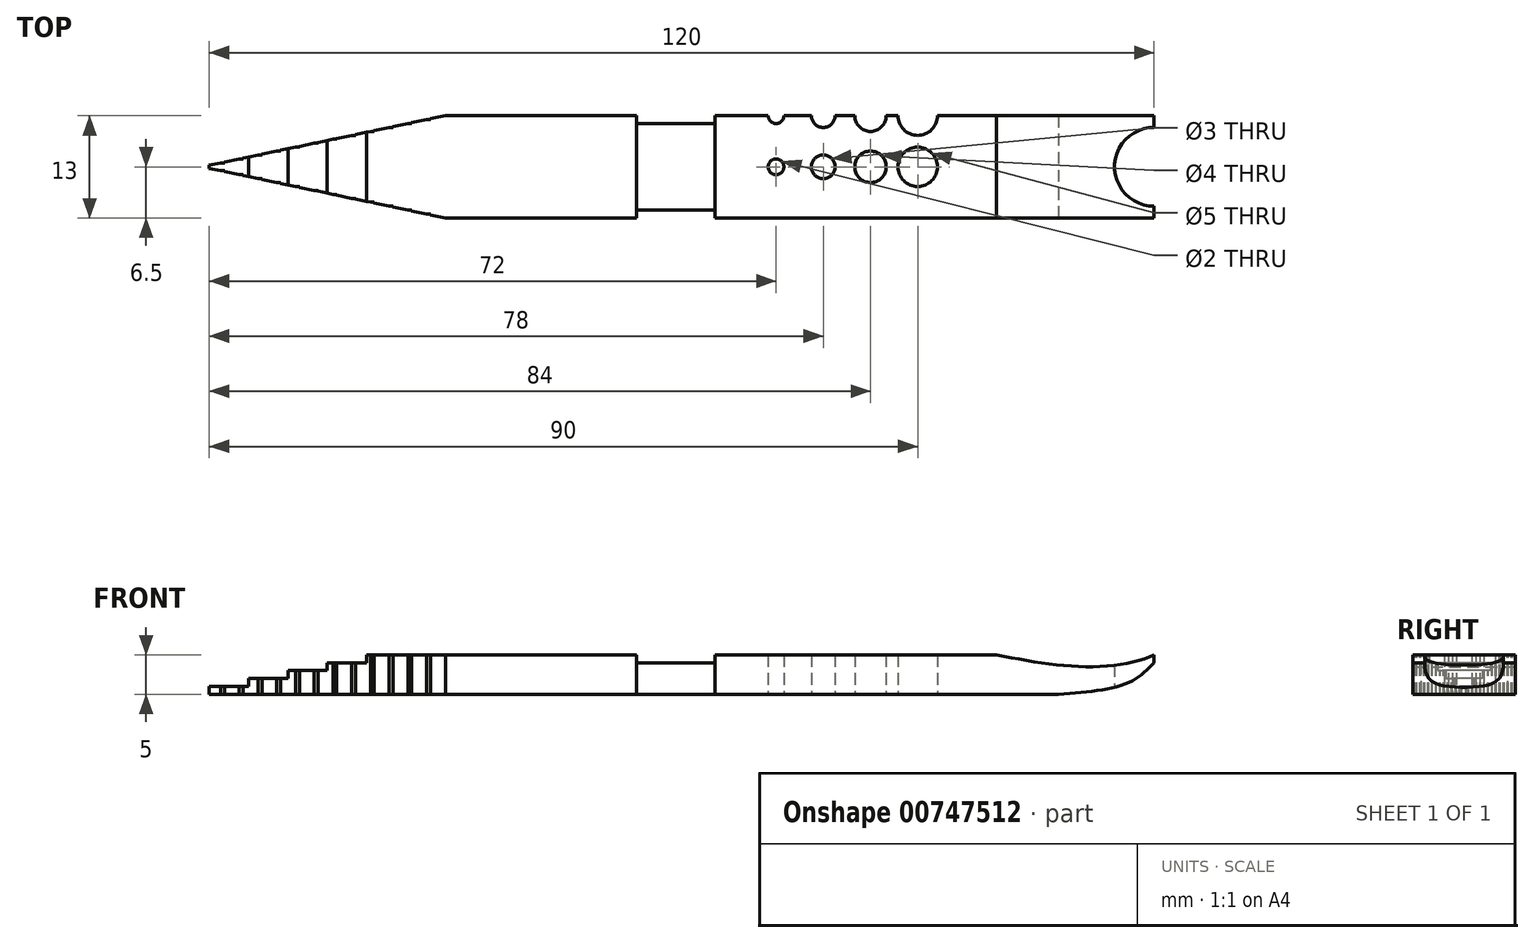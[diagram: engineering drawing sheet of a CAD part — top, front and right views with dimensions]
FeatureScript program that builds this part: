
annotation { "Feature Type Name" : "Feature", "Feature Type Description" : "" }
export const myFeature = defineFeature(function(context is Context, id is Id, definition is map)
    precondition{}
    {
        {
            var Q0;
            Q0=qCreatedBy(makeId("Top.planeOp"),FACE);
            var sketch = newSketch(context, id + "F0", { "sketchPlane" : qUnion([Q0])});
            skLineSegment(sketch, "E0.bottom", {"start": v(0, 0) * mm, "end": v(-20, 0) * mm});
            skLineSegment(sketch, "E0.top", {"start": v(0, -13) * mm, "end": v(-20, -13) * mm});
            skLineSegment(sketch, "E0.left", {"start": v(0, 0) * mm, "end": v(0, -13) * mm});
            skLineSegment(sketch, "E0.right", {"start": v(-20, 0) * mm, "end": v(-20, -13) * mm});
            skLineSegment(sketch, "E1.bottom", {"start": v(0, 0) * mm, "end": v(51, 0) * mm});
            skLineSegment(sketch, "E1.top", {"start": v(0, -13) * mm, "end": v(80, -13) * mm});
            skLineSegment(sketch, "E1.right", {"start": v(80, 0) * mm, "end": v(80, -13) * mm});
            skLineSegment(sketch, "E2.bottom", {"start": v(80, 0) * mm, "end": v(100, 0) * mm});
            skLineSegment(sketch, "E2.top", {"start": v(80, -13) * mm, "end": v(100, -13) * mm});
            skLineSegment(sketch, "E2.right", {"start": v(100, 0) * mm, "end": v(100, -1.5) * mm});
            skLineSegment(sketch, "E3", {"start": v(0, -6.5) * mm, "end": v(80, -6.5) * mm, "construction": true});
            skLineSegment(sketch, "E4.0", {"start": v(70, 0) * mm, "end": v(70, -13) * mm, "construction": true});
            skLineSegment(sketch, "E5.0", {"start": v(64, 0) * mm, "end": v(64, -13) * mm, "construction": true});
            skLineSegment(sketch, "E6.0", {"start": v(58, 0) * mm, "end": v(58, -13) * mm, "construction": true});
            skLineSegment(sketch, "E7.0", {"start": v(52, 0) * mm, "end": v(52, -13) * mm, "construction": true});
            skCircle(sketch, "E8", {"center": v(70, -6.5) * mm, "radius": 2.5 * mm});
            skCircle(sketch, "E9", {"center": v(64, -6.5) * mm, "radius": 2 * mm});
            skCircle(sketch, "E10", {"center": v(58, -6.5) * mm, "radius": 1.5 * mm});
            skCircle(sketch, "E11", {"center": v(52, -6.5) * mm, "radius": 1 * mm});
            skArc(sketch, "E12", {"start": v(67.5, 0) * mm, "mid": v(70, -2.5) * mm, "end": v(72.5, 0) * mm});
            skArc(sketch, "E13", {"start": v(62, 0) * mm, "mid": v(64, -2) * mm, "end": v(66, 0) * mm});
            skArc(sketch, "E14", {"start": v(56.5, 0) * mm, "mid": v(58, -1.5) * mm, "end": v(59.5, 0) * mm});
            skArc(sketch, "E15", {"start": v(51, 0) * mm, "mid": v(52, -1) * mm, "end": v(53, 0) * mm});
            skLineSegment(sketch, "E16.trimOffspring", {"start": v(72.5, 0) * mm, "end": v(80, 0) * mm});
            skLineSegment(sketch, "E17.trimOffspring", {"start": v(66, 0) * mm, "end": v(67.5, 0) * mm});
            skLineSegment(sketch, "E18.trimOffspring", {"start": v(59.5, 0) * mm, "end": v(62, 0) * mm});
            skLineSegment(sketch, "E19.trimOffspring", {"start": v(53, 0) * mm, "end": v(56.5, 0) * mm});
            skArc(sketch, "E20", {"start": v(100, -1.5) * mm, "mid": v(95, -6.5) * mm, "end": v(100, -11.5) * mm});
            skLineSegment(sketch, "E21.trimOffspring", {"start": v(100, -11.5) * mm, "end": v(100, -13) * mm});
            skSolve(sketch);
        }
        {
            var Q0;
            Q0=makeQuery(id+"F0.imprint","IMPRINT",FACE,{"disambiguationData":[TD([[makeQuery(id+"F0.imprint","IMPRINT",EDGE,{"derivedFrom":sQuery(id+"F0.wireOp",EDGE,"E1.bottom")}),-1.0]])]});
            var Q1;
            Q1=makeQuery(id+"F0.imprint","IMPRINT",FACE,{"disambiguationData":[TD([[makeQuery(id+"F0.imprint","IMPRINT",EDGE,{"derivedFrom":sQuery(id+"F0.wireOp",EDGE,"E0.bottom")}),1.0]])]});
            extrude(context, id + "F1", {"entities" : qUnion([Q0, Q1]), "depth" : 5 * mm, "offsetDistance" : 25 * mm});
        }
        {
            var Q0;
            Q0=makeQuery(id+"F0.imprint","IMPRINT",FACE,{"disambiguationData":[TD([[makeQuery(id+"F0.imprint","IMPRINT",EDGE,{"derivedFrom":sQuery(id+"F0.wireOp",EDGE,"E2.bottom")}),-1.0]])]});
            extrude(context, id + "F2", {"entities" : qUnion([Q0]), "operationType" : NewBodyOperationType.ADD, "depth" : 5 * mm, "offsetDistance" : 25 * mm});
        }
        {
            var Q0;
            Q0=makeQuery(id+"F2.boolean.opBoolean","MERGE",FACE,{"derivedFrom":[makeQuery(id+"F1.opExtrude","SWEPT_FACE",FACE,{"disambiguationData":[OSD([sQuery(id+"F0.wireOp",EDGE,"E0.top"),sQuery(id+"F0.wireOp",EDGE,"E1.top")])]}),makeQuery(id+"F2.opExtrude","SWEPT_FACE",FACE,{"disambiguationData":[OSD([sQuery(id+"F0.wireOp",EDGE,"E2.top")])]})]});
            var sketch = newSketch(context, id + "F3", { "sketchPlane" : qUnion([Q0])});
            skLineSegment(sketch, "E22", {"start": v(5, 5) * mm, "end": v(0, 5) * mm});
            skLineSegment(sketch, "E23", {"start": v(0, 5) * mm, "end": v(0, 4) * mm});
            skLineSegment(sketch, "E24", {"start": v(0, 4) * mm, "end": v(-5, 4) * mm});
            skLineSegment(sketch, "E25", {"start": v(-5, 4) * mm, "end": v(-5, 3) * mm});
            skLineSegment(sketch, "E26", {"start": v(-5, 3) * mm, "end": v(-10, 3) * mm});
            skLineSegment(sketch, "E27", {"start": v(-10, 3) * mm, "end": v(-10, 2) * mm});
            skLineSegment(sketch, "E28", {"start": v(-10, 2) * mm, "end": v(-15, 2) * mm});
            skLineSegment(sketch, "E29", {"start": v(-15, 2) * mm, "end": v(-15, 1) * mm});
            skLineSegment(sketch, "E30", {"start": v(-15, 1) * mm, "end": v(-20, 1) * mm});
            skLineSegment(sketch, "E31", {"start": v(-20, 1) * mm, "end": v(-20, 0) * mm});
            skLineSegment(sketch, "E32", {"start": v(-20, 0) * mm, "end": v(0, 0) * mm});
            skLineSegment(sketch, "E33", {"start": v(0, 0) * mm, "end": v(0, -1.18) * mm});
            skLineSegment(sketch, "E34", {"start": v(0, -1.18) * mm, "end": v(-22.5, -1.18) * mm});
            skLineSegment(sketch, "E35", {"start": v(-22.5, -1.18) * mm, "end": v(-22.5, 6.94) * mm});
            skLineSegment(sketch, "E36", {"start": v(-22.5, 6.94) * mm, "end": v(5, 6.94) * mm});
            skLineSegment(sketch, "E37", {"start": v(5, 6.94) * mm, "end": v(5, 5) * mm});
            skLineSegment(sketch, "E38", {"start": v(0, 0) * mm, "end": v(80, 0) * mm, "construction": true});
            skLineSegment(sketch, "E39", {"start": v(80, 0) * mm, "end": v(80, 5) * mm, "construction": true});
            skFitSpline(sketch, "E40", {"points": [v(80, 5) * mm, v(91.86, 3.5) * mm, v(100, 5) * mm, v(102.7, 7.03) * mm], "startDerivative": vector(28.47, -5.44) * mm, "endDerivative": vector(9.91, 9.63) * mm});
            skLineSegment(sketch, "E41", {"start": v(100, 5) * mm, "end": v(100, 4) * mm});
            skLineSegment(sketch, "E42", {"start": v(80, 0) * mm, "end": v(87.86, 0) * mm});
            skFitSpline(sketch, "E43", {"points": [v(87.86, 0) * mm, v(96.6, 1.4) * mm, v(100, 4) * mm, v(102.7, 7.03) * mm], "startDerivative": vector(23.43, 1.75) * mm, "endDerivative": vector(9.4, 10.76) * mm});
            skLineSegment(sketch, "E44", {"start": v(80, 5) * mm, "end": v(80, 7.9) * mm});
            skLineSegment(sketch, "E45", {"start": v(80, 7.9) * mm, "end": v(104.35, 7.9) * mm});
            skLineSegment(sketch, "E46", {"start": v(104.35, 7.9) * mm, "end": v(104.35, -1.83) * mm});
            skLineSegment(sketch, "E47", {"start": v(104.35, -1.83) * mm, "end": v(80, -1.83) * mm});
            skLineSegment(sketch, "E48", {"start": v(80, 0) * mm, "end": v(80, -1.83) * mm});
            skSolve(sketch);
        }
        {
            var Q0;
            {var subQ0=sQuery(id+"F3.wireOp",EDGE,"E41");Q0=makeQuery(id+"F3.imprint","IMPRINT",FACE,{"disambiguationData":[TD([[makeQuery(id+"F3.imprint","IMPRINT",EDGE,{"derivedFrom":subQ0}),1.0]])]});}
            var Q1;
            {var subQ0=sQuery(id+"F3.wireOp",EDGE,"E23");Q1=makeQuery(id+"F3.imprint","IMPRINT",FACE,{"disambiguationData":[TD([[makeQuery(id+"F3.imprint","IMPRINT",EDGE,{"derivedFrom":subQ0}),-1.0]])]});}
            var Q2;
            {var subQ0=sQuery(id+"F3.wireOp",EDGE,"E40");var subQ1=makeQuery(id+"F2.boolean.opBoolean","MERGE",EDGE,{"derivedFrom":[makeQuery(id+"F1.opExtrude","CAP_EDGE",EDGE,{"disambiguationData":[OSD([sQuery(id+"F0.wireOp",EDGE,"E0.top"),sQuery(id+"F0.wireOp",EDGE,"E1.top")])],"isStart":false}),makeQuery(id+"F2.opExtrude","CAP_EDGE",EDGE,{"disambiguationData":[OSD([sQuery(id+"F0.wireOp",EDGE,"E2.top")])],"isStart":false})]});var subQ2=makeQuery(id+"F3.imprint","INTERSECT",VERTEX,{"derivedFrom":[subQ1,subQ0,sQuery(id+"F3.wireOp",EDGE,"E41")]});Q2=makeQuery(id+"F3.imprint","IMPRINT",FACE,{"disambiguationData":[TD([[makeQuery(id+"F3.imprint","IMPRINT",EDGE,{"disambiguationData":[TD([[subQ2,1.0]])],"derivedFrom":subQ0}),1.0]])]});}
            var Q3;
            {var subQ0=sQuery(id+"F3.wireOp",EDGE,"E43");var subQ1=sQuery(id+"F0.wireOp",EDGE,"E2.top");var subQ2=makeQuery(id+"F2.opExtrude","SWEPT_EDGE",EDGE,{"disambiguationData":[OSD([subQ1,sQuery(id+"F0.wireOp",EDGE,"E21.trimOffspring")])]});var subQ3=makeQuery(id+"F3.imprint","INTERSECT",VERTEX,{"derivedFrom":[subQ2,sQuery(id+"F3.wireOp",EDGE,"E41"),subQ0]});Q3=makeQuery(id+"F3.imprint","IMPRINT",FACE,{"disambiguationData":[TD([[makeQuery(id+"F3.imprint","IMPRINT",EDGE,{"disambiguationData":[TD([[subQ3,1.0]])],"derivedFrom":subQ0}),-1.0]])]});}
            extrude(context, id + "F4", {"entities" : qUnion([Q0, Q1, Q2, Q3]), "operationType" : NewBodyOperationType.REMOVE, "oppositeDirection" : true, "depth" : 25 * mm, "offsetDistance" : 25 * mm});
        }
        {
            var Q0;
            Q0=makeQuery(id+"F4.boolean.opBoolean","COPY",FACE,{"derivedFrom":makeQuery(id+"F4.opExtrude","SWEPT_FACE",FACE,{"disambiguationData":[OSD([sQuery(id+"F3.wireOp",EDGE,"E30")])]})});
            var sketch = newSketch(context, id + "F5", { "sketchPlane" : qUnion([Q0])});
            skLineSegment(sketch, "E49", {"start": v(10, -6.5) * mm, "end": v(10, 0) * mm, "construction": true});
            skLineSegment(sketch, "E50", {"start": v(10, -6.5) * mm, "end": v(10, -13) * mm, "construction": true});
            skLineSegment(sketch, "E51", {"start": v(10, 0) * mm, "end": v(8.12, -0.4) * mm});
            skLineSegment(sketch, "E52", {"start": v(10, 0) * mm, "end": v(10, 3.1) * mm});
            skLineSegment(sketch, "E53", {"start": v(10, 3.1) * mm, "end": v(-21.73, 3.1) * mm});
            skLineSegment(sketch, "E54", {"start": v(-21.73, 3.1) * mm, "end": v(-21.73, -15.95) * mm});
            skLineSegment(sketch, "E55", {"start": v(-21.73, -15.95) * mm, "end": v(10, -15.95) * mm});
            skLineSegment(sketch, "E56", {"start": v(10, -15.95) * mm, "end": v(10, -13) * mm});
            skLineSegment(sketch, "E57", {"start": v(-18.57, -6) * mm, "end": v(-18.07, -6) * mm});
            skLineSegment(sketch, "E58", {"start": v(-18.07, -6) * mm, "end": v(-18.07, -5.9) * mm});
            skLineSegment(sketch, "E59", {"start": v(-16.2, -5.5) * mm, "end": v(-15.7, -5.5) * mm});
            skLineSegment(sketch, "E60", {"start": v(-15.7, -5.5) * mm, "end": v(-15.7, -5.4) * mm});
            skLineSegment(sketch, "E61", {"start": v(-13.8, -5) * mm, "end": v(-13.3, -5) * mm});
            skLineSegment(sketch, "E62", {"start": v(-13.3, -5) * mm, "end": v(-13.3, -4.9) * mm});
            skLineSegment(sketch, "E63", {"start": v(-11.43, -4.5) * mm, "end": v(-10.93, -4.5) * mm});
            skLineSegment(sketch, "E64", {"start": v(-10.93, -4.5) * mm, "end": v(-10.93, -4.4) * mm});
            skLineSegment(sketch, "E65", {"start": v(-9.05, -4) * mm, "end": v(-8.55, -4) * mm});
            skLineSegment(sketch, "E66", {"start": v(-8.55, -4) * mm, "end": v(-8.55, -3.9) * mm});
            skLineSegment(sketch, "E67", {"start": v(-6.67, -3.5) * mm, "end": v(-6.17, -3.5) * mm});
            skLineSegment(sketch, "E68", {"start": v(-6.17, -3.5) * mm, "end": v(-6.17, -3.4) * mm});
            skLineSegment(sketch, "E69", {"start": v(-4.29, -3) * mm, "end": v(-3.79, -3) * mm});
            skLineSegment(sketch, "E70", {"start": v(-3.79, -3) * mm, "end": v(-3.79, -2.9) * mm});
            skLineSegment(sketch, "E71", {"start": v(-1.9, -2.5) * mm, "end": v(-1.4, -2.5) * mm});
            skLineSegment(sketch, "E72", {"start": v(-1.4, -2.5) * mm, "end": v(-1.4, -2.4) * mm});
            skLineSegment(sketch, "E73", {"start": v(0.48, -2) * mm, "end": v(0.98, -2) * mm});
            skLineSegment(sketch, "E74", {"start": v(0.98, -2) * mm, "end": v(0.98, -1.9) * mm});
            skLineSegment(sketch, "E75", {"start": v(2.86, -1.5) * mm, "end": v(3.36, -1.5) * mm});
            skLineSegment(sketch, "E76", {"start": v(3.36, -1.5) * mm, "end": v(3.36, -1.4) * mm});
            skLineSegment(sketch, "E77", {"start": v(5.24, -1) * mm, "end": v(5.74, -1) * mm});
            skLineSegment(sketch, "E78", {"start": v(5.74, -1) * mm, "end": v(5.74, -0.9) * mm});
            skLineSegment(sketch, "E79", {"start": v(7.62, -0.5) * mm, "end": v(8.12, -0.5) * mm});
            skLineSegment(sketch, "E80", {"start": v(8.12, -0.5) * mm, "end": v(8.12, -0.4) * mm});
            skLineSegment(sketch, "E81.trimOffspring", {"start": v(7.62, -0.5) * mm, "end": v(5.74, -0.9) * mm});
            skLineSegment(sketch, "E82.trimOffspring", {"start": v(5.24, -1) * mm, "end": v(3.36, -1.4) * mm});
            skLineSegment(sketch, "E83.trimOffspring", {"start": v(2.86, -1.5) * mm, "end": v(0.98, -1.9) * mm});
            skLineSegment(sketch, "E84.trimOffspring", {"start": v(0.48, -2) * mm, "end": v(-1.4, -2.4) * mm});
            skLineSegment(sketch, "E85.trimOffspring", {"start": v(-1.9, -2.5) * mm, "end": v(-3.79, -2.9) * mm});
            skLineSegment(sketch, "E86.trimOffspring", {"start": v(-4.29, -3) * mm, "end": v(-6.17, -3.4) * mm});
            skLineSegment(sketch, "E87.trimOffspring", {"start": v(-6.67, -3.5) * mm, "end": v(-8.55, -3.9) * mm});
            skLineSegment(sketch, "E88.trimOffspring", {"start": v(-9.05, -4) * mm, "end": v(-10.93, -4.4) * mm});
            skLineSegment(sketch, "E89.trimOffspring", {"start": v(-11.43, -4.5) * mm, "end": v(-13.3, -4.9) * mm});
            skLineSegment(sketch, "E90.trimOffspring", {"start": v(-13.8, -5) * mm, "end": v(-15.7, -5.4) * mm});
            skLineSegment(sketch, "E91.trimOffspring", {"start": v(-16.2, -5.5) * mm, "end": v(-18.07, -5.9) * mm});
            skLineSegment(sketch, "E92.MirrorCS", {"start": v(0.98, -11) * mm, "end": v(0.98, -11.1) * mm});
            skLineSegment(sketch, "E93.MirrorCS", {"start": v(-9.05, -9) * mm, "end": v(-8.55, -9) * mm});
            skLineSegment(sketch, "E94.MirrorCS", {"start": v(-8.55, -9) * mm, "end": v(-8.55, -9.1) * mm});
            skLineSegment(sketch, "E95.MirrorCS", {"start": v(0.48, -11) * mm, "end": v(0.98, -11) * mm});
            skLineSegment(sketch, "E96.MirrorCS", {"start": v(3.36, -11.5) * mm, "end": v(3.36, -11.6) * mm});
            skLineSegment(sketch, "E97.MirrorCS", {"start": v(7.62, -12.5) * mm, "end": v(8.12, -12.5) * mm});
            skLineSegment(sketch, "E98.MirrorCS", {"start": v(5.74, -12) * mm, "end": v(5.74, -12.1) * mm});
            skLineSegment(sketch, "E99.MirrorCS", {"start": v(-10.93, -8.5) * mm, "end": v(-10.93, -8.6) * mm});
            skLineSegment(sketch, "E100.MirrorCS", {"start": v(-1.4, -10.5) * mm, "end": v(-1.4, -10.6) * mm});
            skLineSegment(sketch, "E101.MirrorCS", {"start": v(-18.07, -7) * mm, "end": v(-18.07, -7.1) * mm});
            skLineSegment(sketch, "E102.MirrorCS", {"start": v(8.12, -12.5) * mm, "end": v(8.12, -12.6) * mm});
            skLineSegment(sketch, "E103.MirrorCS", {"start": v(-4.29, -10) * mm, "end": v(-3.79, -10) * mm});
            skLineSegment(sketch, "E104.MirrorCS", {"start": v(-11.43, -8.5) * mm, "end": v(-10.93, -8.5) * mm});
            skLineSegment(sketch, "E105.MirrorCS", {"start": v(-3.79, -10) * mm, "end": v(-3.79, -10.1) * mm});
            skLineSegment(sketch, "E106.MirrorCS", {"start": v(2.86, -11.5) * mm, "end": v(3.36, -11.5) * mm});
            skLineSegment(sketch, "E107.MirrorCS", {"start": v(-15.7, -7.5) * mm, "end": v(-15.7, -7.6) * mm});
            skLineSegment(sketch, "E108.MirrorCS", {"start": v(-13.3, -8) * mm, "end": v(-13.3, -8.1) * mm});
            skLineSegment(sketch, "E109.MirrorCS", {"start": v(-16.2, -7.5) * mm, "end": v(-15.7, -7.5) * mm});
            skLineSegment(sketch, "E110.MirrorCS", {"start": v(-13.8, -8) * mm, "end": v(-13.3, -8) * mm});
            skLineSegment(sketch, "E111.MirrorCS", {"start": v(-6.17, -9.5) * mm, "end": v(-6.17, -9.6) * mm});
            skLineSegment(sketch, "E112.MirrorCS", {"start": v(-1.9, -10.5) * mm, "end": v(-1.4, -10.5) * mm});
            skLineSegment(sketch, "E113.MirrorCS", {"start": v(-6.67, -9.5) * mm, "end": v(-6.17, -9.5) * mm});
            skLineSegment(sketch, "E114.MirrorCS", {"start": v(5.24, -12) * mm, "end": v(5.74, -12) * mm});
            skLineSegment(sketch, "E115.MirrorCS", {"start": v(-18.57, -7) * mm, "end": v(-18.07, -7) * mm});
            skLineSegment(sketch, "E116.MirrorCS", {"start": v(-1.9, -10.5) * mm, "end": v(-3.79, -10.1) * mm});
            skLineSegment(sketch, "E117.MirrorCS", {"start": v(-13.8, -8) * mm, "end": v(-15.7, -7.6) * mm});
            skLineSegment(sketch, "E118.MirrorCS", {"start": v(-4.29, -10) * mm, "end": v(-6.17, -9.6) * mm});
            skLineSegment(sketch, "E119.MirrorCS", {"start": v(5.24, -12) * mm, "end": v(3.36, -11.6) * mm});
            skLineSegment(sketch, "E120.MirrorCS", {"start": v(-16.2, -7.5) * mm, "end": v(-18.07, -7.1) * mm});
            skLineSegment(sketch, "E121.MirrorCS", {"start": v(7.62, -12.5) * mm, "end": v(5.74, -12.1) * mm});
            skLineSegment(sketch, "E122.MirrorCS", {"start": v(0.48, -11) * mm, "end": v(-1.4, -10.6) * mm});
            skLineSegment(sketch, "E123.MirrorCS", {"start": v(-11.43, -8.5) * mm, "end": v(-13.3, -8.1) * mm});
            skLineSegment(sketch, "E124.MirrorCS", {"start": v(10, -13) * mm, "end": v(8.12, -12.6) * mm});
            skLineSegment(sketch, "E125.MirrorCS", {"start": v(2.86, -11.5) * mm, "end": v(0.98, -11.1) * mm});
            skLineSegment(sketch, "E126.MirrorCS", {"start": v(-6.67, -9.5) * mm, "end": v(-8.55, -9.1) * mm});
            skLineSegment(sketch, "E127.MirrorCS", {"start": v(-9.05, -9) * mm, "end": v(-10.93, -8.6) * mm});
            skLineSegment(sketch, "E128", {"start": v(-20, -6.5) * mm, "end": v(-20, -6.25) * mm});
            skLineSegment(sketch, "E129", {"start": v(-20, -6.5) * mm, "end": v(-20, -6.75) * mm});
            skLineSegment(sketch, "E130", {"start": v(-20, -6.75) * mm, "end": v(-18.57, -7) * mm});
            skLineSegment(sketch, "E131", {"start": v(-18.57, -6) * mm, "end": v(-20, -6.25) * mm});
            skSolve(sketch);
        }
        {
            var Q0;
            Q0=makeQuery(id+"F5.imprint","IMPRINT",FACE,{"disambiguationData":[TD([[makeQuery(id+"F5.imprint","IMPRINT",EDGE,{"derivedFrom":sQuery(id+"F5.wireOp",EDGE,"E51")}),-1.0]])]});
            var Q1;
            Q1=makeQuery(id+"F5.imprint","IMPRINT",FACE,{"disambiguationData":[TD([[makeQuery(id+"F5.imprint","IMPRINT",EDGE,{"derivedFrom":sQuery(id+"F5.wireOp",EDGE,"E57")}),1.0]])]});
            var Q2;
            Q2=makeQuery(id+"F5.imprint","IMPRINT",FACE,{"disambiguationData":[TD([[makeQuery(id+"F5.imprint","IMPRINT",EDGE,{"derivedFrom":sQuery(id+"F5.wireOp",EDGE,"E101.MirrorCS")}),-1.0]])]});
            extrude(context, id + "F6", {"entities" : qUnion([Q0, Q1, Q2]), "operationType" : NewBodyOperationType.REMOVE, "oppositeDirection" : true, "depth" : 25 * mm, "offsetDistance" : 25 * mm, "hasSecondDirection" : true, "secondDirectionOppositeDirection" : false, "secondDirectionDepth" : 25 * mm});
        }
        {
            var Q0;
            {var subQ0=sQuery(id+"F0.wireOp",EDGE,"E1.right");Q0=makeQuery(id+"F2.boolean.opBoolean","MERGE",FACE,{"derivedFrom":[makeQuery(id+"F1.opExtrude","CAP_FACE",FACE,{"disambiguationData":[OSD([sQuery(id+"F0.wireOp",EDGE,"E0.bottom"),sQuery(id+"F0.wireOp",EDGE,"E0.top"),sQuery(id+"F0.wireOp",EDGE,"E0.right"),sQuery(id+"F0.wireOp",EDGE,"E1.bottom"),sQuery(id+"F0.wireOp",EDGE,"E1.top"),subQ0,sQuery(id+"F0.wireOp",EDGE,"E8"),sQuery(id+"F0.wireOp",EDGE,"E9"),sQuery(id+"F0.wireOp",EDGE,"E10"),sQuery(id+"F0.wireOp",EDGE,"E11"),sQuery(id+"F0.wireOp",EDGE,"E12"),sQuery(id+"F0.wireOp",EDGE,"E13"),sQuery(id+"F0.wireOp",EDGE,"E14"),sQuery(id+"F0.wireOp",EDGE,"E15"),sQuery(id+"F0.wireOp",EDGE,"E16.trimOffspring"),sQuery(id+"F0.wireOp",EDGE,"E17.trimOffspring"),sQuery(id+"F0.wireOp",EDGE,"E18.trimOffspring"),sQuery(id+"F0.wireOp",EDGE,"E19.trimOffspring")])],"isStart":false}),makeQuery(id+"F2.opExtrude","CAP_FACE",FACE,{"disambiguationData":[OSD([sQuery(id+"F0.wireOp",EDGE,"E2.bottom"),sQuery(id+"F0.wireOp",EDGE,"E2.top"),subQ0,sQuery(id+"F0.wireOp",EDGE,"E2.right"),sQuery(id+"F0.wireOp",EDGE,"E20"),sQuery(id+"F0.wireOp",EDGE,"E21.trimOffspring")])],"isStart":false})]});}
            var sketch = newSketch(context, id + "F7", { "sketchPlane" : qUnion([Q0])});
            skLineSegment(sketch, "E132.bottom", {"start": v(44.27, 0) * mm, "end": v(34.27, 0) * mm});
            skLineSegment(sketch, "E132.top", {"start": v(44.27, -13) * mm, "end": v(34.27, -13) * mm});
            skLineSegment(sketch, "E132.left", {"start": v(44.27, 0) * mm, "end": v(44.27, -13) * mm});
            skLineSegment(sketch, "E132.right", {"start": v(34.27, 0) * mm, "end": v(34.27, -13) * mm});
            skSolve(sketch);
        }
        {
            var Q0;
            Q0=makeQuery(id+"F7.imprint","IMPRINT",FACE,{"disambiguationData":[TD([[makeQuery(id+"F7.imprint","IMPRINT",EDGE,{"derivedFrom":sQuery(id+"F7.wireOp",EDGE,"E132.bottom")}),-1.0]])]});
            extrude(context, id + "F8", {"entities" : qUnion([Q0]), "operationType" : NewBodyOperationType.REMOVE, "oppositeDirection" : true, "depth" : 1 * mm, "offsetDistance" : 25 * mm});
        }
        {
            var Q0;
            Q0=makeQuery(id+"F2.boolean.opBoolean","MERGE",FACE,{"derivedFrom":[makeQuery(id+"F1.opExtrude","SWEPT_FACE",FACE,{"disambiguationData":[OSD([sQuery(id+"F0.wireOp",EDGE,"E0.top"),sQuery(id+"F0.wireOp",EDGE,"E1.top")])]}),makeQuery(id+"F2.opExtrude","SWEPT_FACE",FACE,{"disambiguationData":[OSD([sQuery(id+"F0.wireOp",EDGE,"E2.top")])]})]});
            var sketch = newSketch(context, id + "F9", { "sketchPlane" : qUnion([Q0])});
            skLineSegment(sketch, "E133.bottom", {"start": v(34.27, 4) * mm, "end": v(44.27, 4) * mm});
            skLineSegment(sketch, "E133.top", {"start": v(34.27, 0) * mm, "end": v(44.27, 0) * mm});
            skLineSegment(sketch, "E133.left", {"start": v(34.27, 4) * mm, "end": v(34.27, 0) * mm});
            skLineSegment(sketch, "E133.right", {"start": v(44.27, 4) * mm, "end": v(44.27, 0) * mm});
            skSolve(sketch);
        }
        {
            var Q0;
            Q0=makeQuery(id+"F9.imprint","IMPRINT",FACE,{"disambiguationData":[TD([[makeQuery(id+"F9.imprint","IMPRINT",EDGE,{"derivedFrom":sQuery(id+"F9.wireOp",EDGE,"E133.bottom")}),-1.0]])]});
            extrude(context, id + "F10", {"entities" : qUnion([Q0]), "operationType" : NewBodyOperationType.REMOVE, "oppositeDirection" : true, "depth" : 1 * mm, "offsetDistance" : 25 * mm});
        }
        {
            var Q0;
            Q0=makeQuery(id+"F1.opExtrude","SWEPT_FACE",FACE,{"disambiguationData":[OSD([sQuery(id+"F0.wireOp",EDGE,"E0.bottom"),sQuery(id+"F0.wireOp",EDGE,"E1.bottom")])]});
            var sketch = newSketch(context, id + "F11", { "sketchPlane" : qUnion([Q0])});
            skLineSegment(sketch, "E134.bottom", {"start": v(-44.27, 4) * mm, "end": v(-34.27, 4) * mm});
            skLineSegment(sketch, "E134.top", {"start": v(-44.27, 0) * mm, "end": v(-34.27, 0) * mm});
            skLineSegment(sketch, "E134.left", {"start": v(-44.27, 4) * mm, "end": v(-44.27, 0) * mm});
            skLineSegment(sketch, "E134.right", {"start": v(-34.27, 4) * mm, "end": v(-34.27, 0) * mm});
            skSolve(sketch);
        }
        {
            var Q0;
            Q0=makeQuery(id+"F11.imprint","IMPRINT",FACE,{"disambiguationData":[TD([[makeQuery(id+"F11.imprint","IMPRINT",EDGE,{"derivedFrom":sQuery(id+"F11.wireOp",EDGE,"E134.bottom")}),1.0]])]});
            extrude(context, id + "F12", {"entities" : qUnion([Q0]), "operationType" : NewBodyOperationType.REMOVE, "oppositeDirection" : true, "depth" : 1 * mm, "offsetDistance" : 25 * mm});
        }
    });
